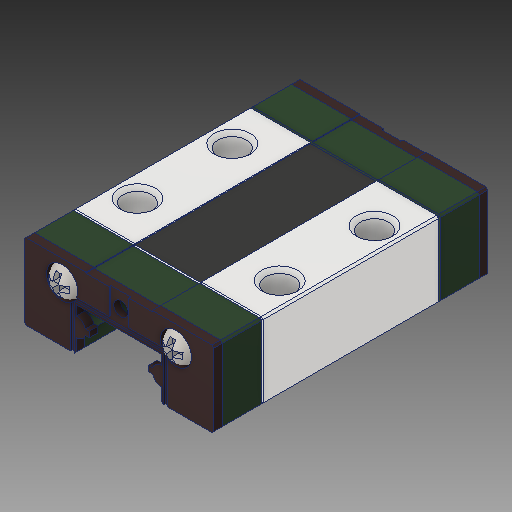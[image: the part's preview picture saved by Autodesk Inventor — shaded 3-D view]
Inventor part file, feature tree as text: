
AUTODESK INVENTOR PART (.ipt)
format: ipt  version: 2019 (Build 230136000, 136)  size: 606,720 bytes
history: imported  units: mm
features: other x7, sketch x2, plane x1, imported_body x1
ambient origin geometry x8: Origin, YZ Plane, XZ Plane, XY Plane, X Axis, Y Axis, Z Axis, Center Point
bodies: Solid1 (imported_parasolid), Solid2 (imported_parasolid), Solid3 (imported_parasolid), Solid4 (imported_parasolid), Solid5 (imported_parasolid)
feature tree (11):
  other  "MGN9C Block.ipt"
  other  "Solid1::MGN9C Block.ipt"
  other  "Solid2::MGN9C Block.ipt"
  other  "Solid3::MGN9C Block.ipt"
  other  "Solid4::MGN9C Block.ipt"
  other  "Solid9::MGN9C Block.ipt"
  other  "TaggingFeature1"
  sketch  "Sketch2"  dims[d0=10.0mm]
  sketch  "Sketch3"
  plane  "Work Plane1"
  imported_body  NMx_Import_Brep_tag  [imported B-rep: ~326 faces, bbox_mm=[20.0, 8.0, 30.285311]]
